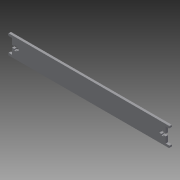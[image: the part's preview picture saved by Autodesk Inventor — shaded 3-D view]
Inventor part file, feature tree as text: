
AUTODESK INVENTOR PART (.ipt)
format: ipt  version: 2013 (Build 170138000, 138)  size: 136,704 bytes
history: native  units: mm
features: extrude x1
ambient origin geometry x8: Origin, YZ Plane, XZ Plane, XY Plane, X Axis, Y Axis, Z Axis, Center Point
bodies: Solid1 (feature_tree)
feature tree (1):
  extrude  "Extrusion1"  Depth=3.0mm
